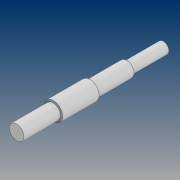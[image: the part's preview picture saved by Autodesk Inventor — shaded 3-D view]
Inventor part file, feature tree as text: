
AUTODESK INVENTOR PART (.ipt)
format: ipt  version: 2021 (Build 250183000, 183)  size: 94,720 bytes
history: native  units: mm
features: revolve x1, sketch x1
ambient origin geometry x8: Origin, YZ Plane, XZ Plane, XY Plane, X Axis, Y Axis, Z Axis, Center Point
bodies: Solid1 (feature_tree)
feature tree (2):
  revolve  "Revolution1"  [1 undecoded]
  sketch  "Sketch1"  dims[d0=3.0mm d1=80.0mm d2=60.0mm d3=20.0mm d4=4.0mm d5=5.0mm d6=90.0deg]
note: 1 required parameter value undecoded (feature->parameter linkage not recoverable at this tier; creation-order binding heuristic only, values carry confidence <= 0.55)
